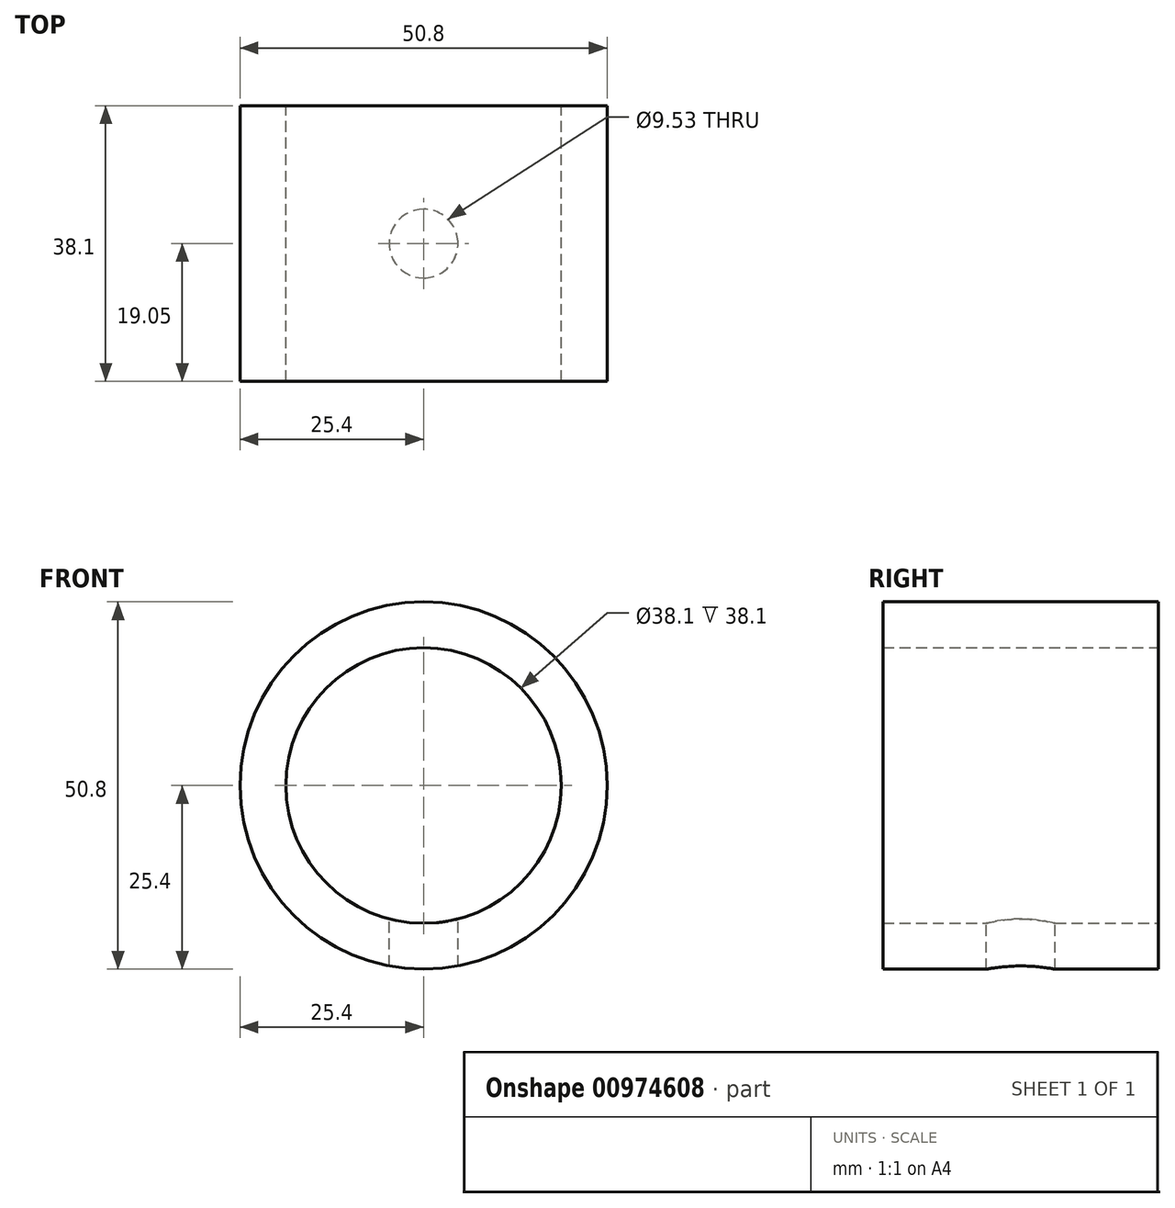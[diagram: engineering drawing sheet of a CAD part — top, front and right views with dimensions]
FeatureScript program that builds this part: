
annotation { "Feature Type Name" : "Feature", "Feature Type Description" : "" }
export const myFeature = defineFeature(function(context is Context, id is Id, definition is map)
    precondition{}
    {
        {
            var Q0;
            Q0=qCreatedBy(makeId("Front.planeOp"),FACE);
            var sketch = newSketch(context, id + "F0", { "sketchPlane" : qUnion([Q0])});
            skCircle(sketch, "E0", {"center": v(0, 0) * mm, "radius": 19.05 * mm});
            skCircle(sketch, "E1", {"center": v(0, 0) * mm, "radius": 25.4 * mm});
            skSolve(sketch);
        }
        {
            var Q0;
            Q0 = qSketchRegion(id + "F0", true);
            extrude(context, id + "F1", {"entities" : qUnion([Q0]), "depth" : 38.1 * mm, "offsetDistance" : 25.4 * mm});
        }
        {
            var Q0;
            Q0=qCreatedBy(makeId("Top.planeOp"),FACE);
            var sketch = newSketch(context, id + "F2", { "sketchPlane" : qUnion([Q0])});
            skCircle(sketch, "E2", {"center": v(0, -19.05) * mm, "radius": 4.76 * mm});
            skSolve(sketch);
        }
        {
            var Q0;
            Q0 = qSketchRegion(id + "F2", true);
            extrude(context, id + "F3", {"entities" : qUnion([Q0]), "operationType" : NewBodyOperationType.REMOVE, "oppositeDirection" : true, "depth" : 25.4 * mm, "offsetDistance" : 25.4 * mm});
        }
    });
